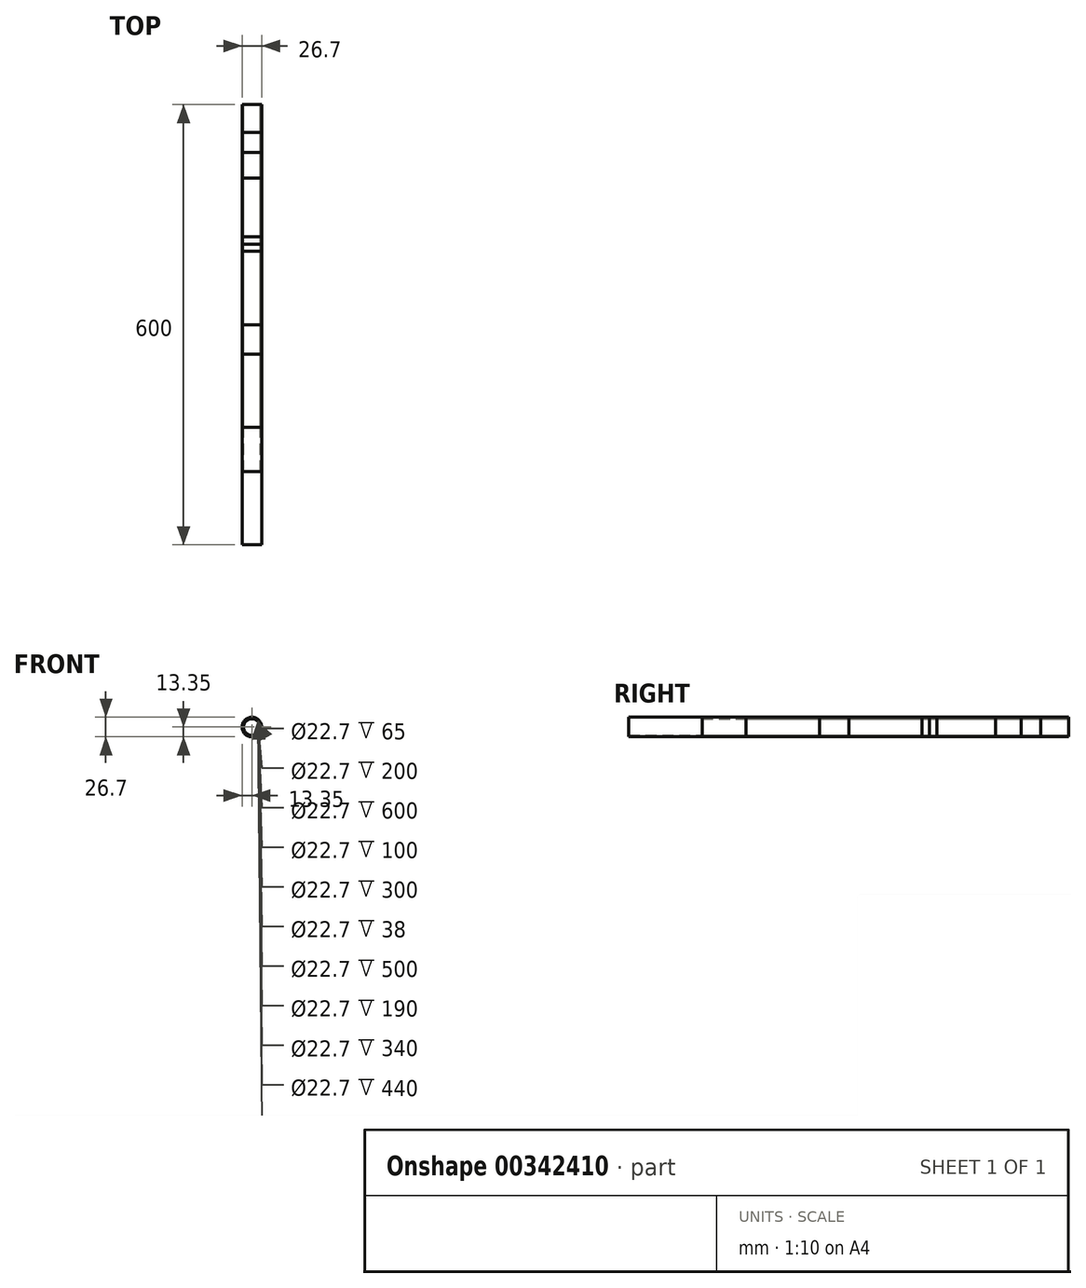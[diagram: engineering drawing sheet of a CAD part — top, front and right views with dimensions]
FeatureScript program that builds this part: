
annotation { "Feature Type Name" : "Feature", "Feature Type Description" : "" }
export const myFeature = defineFeature(function(context is Context, id is Id, definition is map)
    precondition{}
    {
        {
            var Q0;
            Q0=qCreatedBy(makeId("Front.planeOp"),FACE);
            var sketch = newSketch(context, id + "F0", { "sketchPlane" : qUnion([Q0])});
            skCircle(sketch, "E0", {"center": v(0, 0) * mm, "radius": 13.35 * mm});
            skCircle(sketch, "E1", {"center": v(0, 0) * mm, "radius": 11.35 * mm});
            skSolve(sketch);
        }
        {
            var Q0;
            Q0=makeQuery(id+"F0.imprint","IMPRINT",FACE,{"disambiguationData":[TD([[makeQuery(id+"F0.imprint","IMPRINT",EDGE,{"derivedFrom":sQuery(id+"F0.wireOp",EDGE,"E0")}),1.0]])]});
            extrude(context, id + "F1", {"entities" : qUnion([Q0]), "depth" : 500 * mm});
        }
        {
            var Q0;
            Q0=makeQuery(id+"F0.imprint","IMPRINT",FACE,{"disambiguationData":[TD([[makeQuery(id+"F0.imprint","IMPRINT",EDGE,{"derivedFrom":sQuery(id+"F0.wireOp",EDGE,"E0")}),1.0]])]});
            extrude(context, id + "F2", {"entities" : qUnion([Q0]), "depth" : 300 * mm});
        }
        {
            var Q0;
            Q0 = qSketchRegion(id + "F0", true);
            extrude(context, id + "F3", {"entities" : qUnion([Q0]), "depth" : 38 * mm});
        }
        {
            var Q0;
            Q0=makeQuery(id+"F0.imprint","IMPRINT",FACE,{"disambiguationData":[TD([[makeQuery(id+"F0.imprint","IMPRINT",EDGE,{"derivedFrom":sQuery(id+"F0.wireOp",EDGE,"E0")}),1.0]])]});
            extrude(context, id + "F4", {"entities" : qUnion([Q0]), "depth" : 600 * mm});
        }
        {
            var Q0;
            Q0=makeQuery(id+"F0.imprint","IMPRINT",FACE,{"disambiguationData":[TD([[makeQuery(id+"F0.imprint","IMPRINT",EDGE,{"derivedFrom":sQuery(id+"F0.wireOp",EDGE,"E0")}),1.0]])]});
            extrude(context, id + "F5", {"entities" : qUnion([Q0]), "depth" : 100 * mm});
        }
        {
            var Q0;
            Q0 = qSketchRegion(id + "F0", true);
            extrude(context, id + "F6", {"entities" : qUnion([Q0]), "depth" : 65 * mm});
        }
        {
            var Q0;
            Q0=makeQuery(id+"F0.imprint","IMPRINT",FACE,{"disambiguationData":[TD([[makeQuery(id+"F0.imprint","IMPRINT",EDGE,{"derivedFrom":sQuery(id+"F0.wireOp",EDGE,"E0")}),1.0]])]});
            extrude(context, id + "F7", {"entities" : qUnion([Q0]), "depth" : 200 * mm});
        }
        {
            var Q0;
            Q0=makeQuery(id+"F0.imprint","IMPRINT",FACE,{"disambiguationData":[TD([[makeQuery(id+"F0.imprint","IMPRINT",EDGE,{"derivedFrom":sQuery(id+"F0.wireOp",EDGE,"E0")}),1.0]])]});
            extrude(context, id + "F8", {"entities" : qUnion([Q0]), "depth" : 440 * mm});
        }
        {
            var Q0;
            Q0=makeQuery(id+"F0.imprint","IMPRINT",FACE,{"disambiguationData":[TD([[makeQuery(id+"F0.imprint","IMPRINT",EDGE,{"derivedFrom":sQuery(id+"F0.wireOp",EDGE,"E0")}),1.0]])]});
            extrude(context, id + "F9", {"entities" : qUnion([Q0]), "depth" : 180 * mm});
        }
        {
            var Q0;
            Q0=makeQuery(id+"F0.imprint","IMPRINT",FACE,{"disambiguationData":[TD([[makeQuery(id+"F0.imprint","IMPRINT",EDGE,{"derivedFrom":sQuery(id+"F0.wireOp",EDGE,"E0")}),1.0]])]});
            extrude(context, id + "F10", {"entities" : qUnion([Q0]), "depth" : 190 * mm});
        }
        {
            var Q0;
            Q0=makeQuery(id+"F0.imprint","IMPRINT",FACE,{"disambiguationData":[TD([[makeQuery(id+"F0.imprint","IMPRINT",EDGE,{"derivedFrom":sQuery(id+"F0.wireOp",EDGE,"E0")}),1.0]])]});
            extrude(context, id + "F11", {"entities" : qUnion([Q0]), "depth" : 340 * mm});
        }
    });
